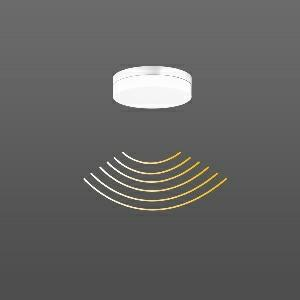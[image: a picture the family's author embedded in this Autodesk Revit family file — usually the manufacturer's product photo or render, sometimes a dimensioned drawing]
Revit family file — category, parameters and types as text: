
# Revit family: flat_slim_round_312135_002_19_4575
name_source: partatom
category: Lighting Fixtures
units: mm (PartAtom-declared; Revit-internal decimal feet)

## family parameters
Cut with Voids When Loaded = No
Host = Face
Light Source = No
Part Type = Normal
Room Calculation Point = No
Round Connector Dimension = Use Diameter
Shared = No

## types (1)
- FLAT SLIM round (1 x LED Modul 830, 1150 lm, 3000)
    Apparent Load = 12 VA
    CIE Flux Codes = 43 74 92 91 100
    Color Rendering = 80
    Color Temperature = 3000
    Default Elevation = 1800 mm
    Height = 63 mm
    Lamp = 1 x LED Modul 830
    Lamp Light Flux = 1150 lm
    Lamp count = 1
    Length = 230 mm
    Lifetime = 50000 h
    Luminous efficacy = 96 lm/W
    Manufacturer = RZB
    ModVariant = No
    Model = 312135.002.19
    Mounting Place = Wall, Ceiling
    Mounting Type = Surface mounted
    Number of Poles = 1
    OnlyDefault = Yes
    Power Factor = 1
    Product Name = FLAT SLIM round
    Product group = Surface mounted ceiling and wall luminaires
    ProductGroupID = 305
    Protection Class = Protection class I
    Protection Degree = IP 65
    RLX_Detail_Level = 1
    RLX_Emergency_Light_Flux = 0 lm
    RLX_Emergency_Type = 0
    RLX_Emergency_Type_DB = No
    RlxData = <blob elided: 32053 chars, md5=9cb3d0b3>
    Socket = socket
    Standby Power = 0 W
    System Light Flux = 1150 lm
    System Power = 12 W
    Type Comments = Product without accessories
    Type Image = 312132.002.19.jpg
    URL = http://relux.com
    VarID = ---
    Voltage = 230 V
    Voltage Range = 220-240 V
    Weight = 0.00 kg
    Width = 0 mm  [stored 0 ft]

note: [stored X ft] marks values corroborated as IEEE doubles in the binary element streams (Revit-internal decimal feet)

## geometry (parser evidence)
native form markers: Blend x4, Sweep x11
no freeform markers — native parametric forms only
